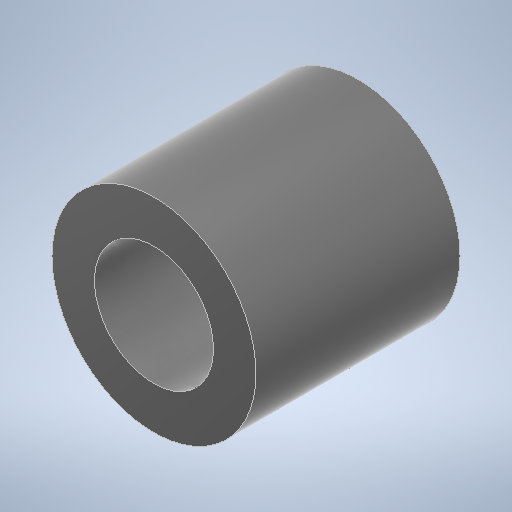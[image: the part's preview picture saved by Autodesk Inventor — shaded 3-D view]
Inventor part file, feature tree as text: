
AUTODESK INVENTOR PART (.ipt)
format: ipt  version: 2025.1 (Build 291241020, 241B)  size: 361,472 bytes
history: native  units: mm
features: extrude x1, sketch x1
ambient origin geometry x8: Origin, YZ Plane, XZ Plane, XY Plane, X Axis, Y Axis, Z Axis, Center Point
bodies: Solid1 (feature_tree)
feature tree (2):
  extrude  "Extrusion1"  Depth=6.0mm
  sketch  "Sketch1"  dims[d0=6.0mm d1=3.5mm d2=6.0mm d3=0.0mm]
